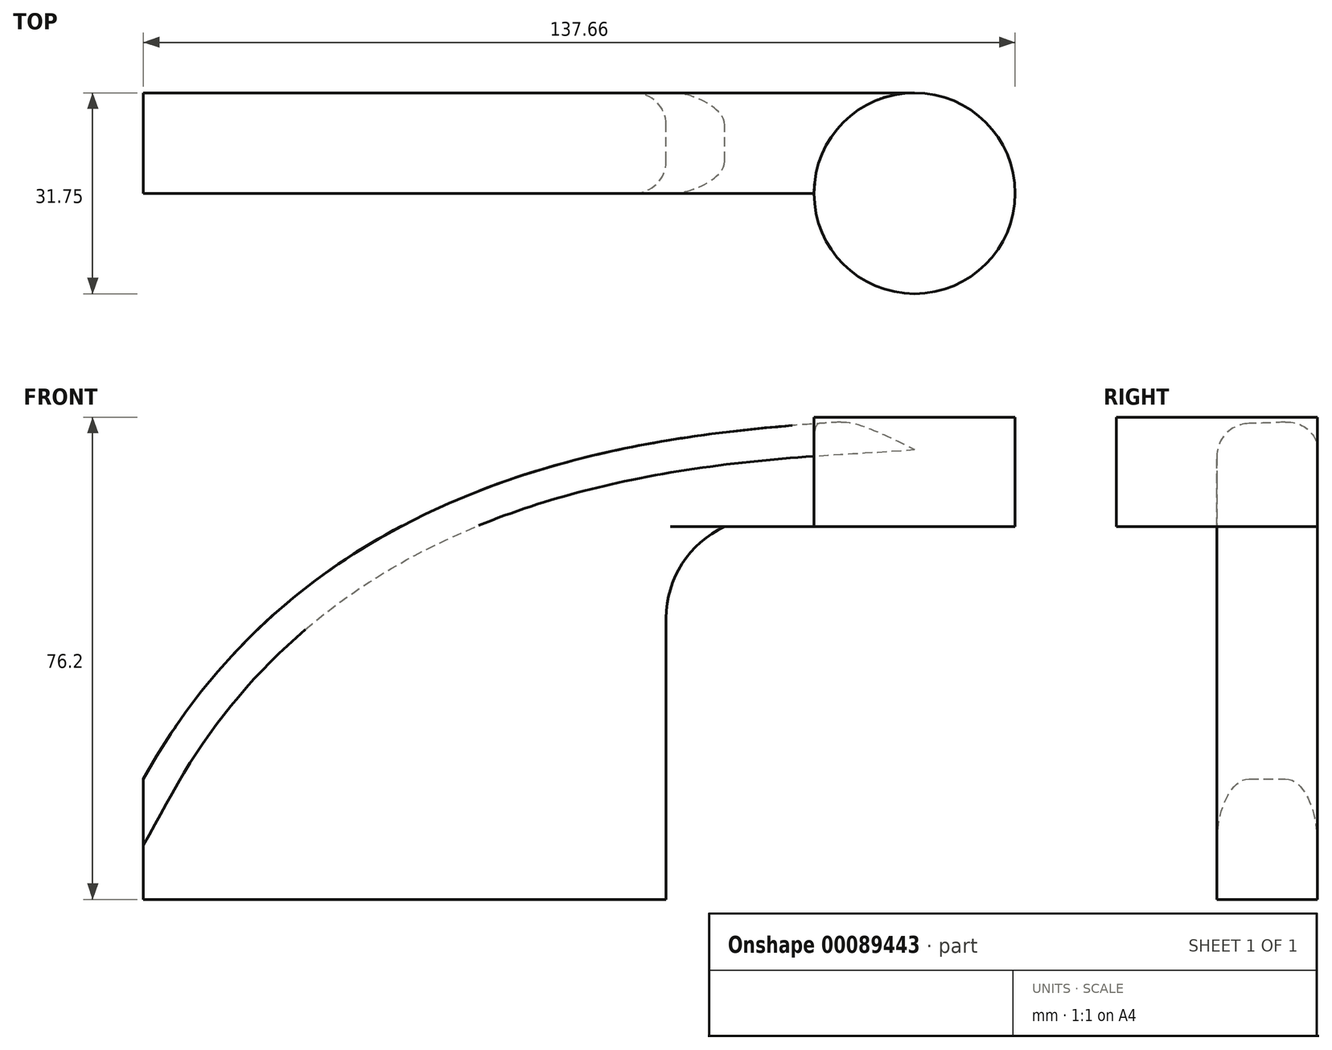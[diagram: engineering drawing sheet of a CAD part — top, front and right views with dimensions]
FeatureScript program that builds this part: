
annotation { "Feature Type Name" : "Feature", "Feature Type Description" : "" }
export const myFeature = defineFeature(function(context is Context, id is Id, definition is map)
    precondition{}
    {
        {
            var Q0;
            Q0=qCreatedBy(makeId("Front.planeOp"),FACE);
            var sketch = newSketch(context, id + "F0", { "sketchPlane" : qUnion([Q0])});
            skLineSegment(sketch, "E0.bottom", {"start": v(-87.78, -32.74) * mm, "end": v(-5.23, -32.74) * mm});
            skLineSegment(sketch, "E0.top", {"start": v(-87.78, -13.69) * mm, "end": v(-5.23, -13.69) * mm});
            skLineSegment(sketch, "E0.left", {"start": v(-87.78, -32.74) * mm, "end": v(-87.78, -13.69) * mm});
            skLineSegment(sketch, "E0.right", {"start": v(-5.23, -32.74) * mm, "end": v(-5.23, -13.69) * mm});
            skLineSegment(sketch, "E1.bottom", {"start": v(84.8, 43.46) * mm, "end": v(34, 43.46) * mm});
            skLineSegment(sketch, "E1.top", {"start": v(84.8, 11.71) * mm, "end": v(34, 11.71) * mm});
            skLineSegment(sketch, "E1.left", {"start": v(84.8, 43.46) * mm, "end": v(84.8, 11.71) * mm});
            skLineSegment(sketch, "E1.right", {"start": v(34, 43.46) * mm, "end": v(34, 11.71) * mm});
            skPoint(sketch, "E1.middle", {"position": v(59.4, 27.59) * mm});
            skLineSegment(sketch, "E2", {"start": v(-5.23, -13.69) * mm, "end": v(-5.23, 11.71) * mm});
            skLineSegment(sketch, "E3", {"start": v(69.71, 19.66) * mm, "end": v(111.85, 19.66) * mm});
            skPoint(sketch, "E4.startSnap0", {"position": v(34, 27.59) * mm});
            skArc(sketch, "E5", {"start": v(-5.23, 11.71) * mm, "mid": v(-2.71, 20.29) * mm, "end": v(4.04, 26.15) * mm});
            skLineSegment(sketch, "E6", {"start": v(4.04, 26.15) * mm, "end": v(48.1, 26.15) * mm});
            skLineSegment(sketch, "E7.0", {"start": v(0.72, 45.2) * mm, "end": v(48.1, 45.2) * mm});
            skArc(sketch, "E7.1", {"start": v(-24.28, 11.71) * mm, "mid": v(-17.34, 32.6) * mm, "end": v(0.72, 45.2) * mm});
            skLineSegment(sketch, "E7.2", {"start": v(-24.28, -13.69) * mm, "end": v(-24.28, 11.71) * mm});
            skLineSegment(sketch, "E8", {"start": v(48.1, 11.71) * mm, "end": v(48.1, 45.2) * mm});
            skFitSpline(sketch, "E9", {"points": [v(-87.78, -13.69) * mm, v(34, 43.46) * mm, v(48.1, 45.2) * mm], "startDerivative": vector(126, 227.65) * mm, "endDerivative": vector(44.75, -1.35) * mm});
            skSolve(sketch);
        }
        {
            var Q0;
            Q0=makeQuery(id+"F0.imprint","IMPRINT",FACE,{"disambiguationData":[TD([[makeQuery(id+"F0.imprint","IMPRINT",EDGE,{"derivedFrom":sQuery(id+"F0.wireOp",EDGE,"E0.bottom")}),1.0]])]});
            var Q1;
            {var subQ1=sQuery(id+"F0.wireOp",EDGE,"E2");Q1=makeQuery(id+"F0.imprint","IMPRINT",FACE,{"disambiguationData":[TD([[makeQuery(id+"F0.imprint","IMPRINT",EDGE,{"derivedFrom":subQ1}),1.0]])]});}
            var Q2;
            {var subQ3=sQuery(id+"F0.wireOp",EDGE,"E7.2");Q2=makeQuery(id+"F0.imprint","IMPRINT",FACE,{"disambiguationData":[TD([[makeQuery(id+"F0.imprint","IMPRINT",EDGE,{"derivedFrom":subQ3}),1.0]])]});}
            extrude(context, id + "F1", {"entities" : qUnion([Q0, Q1, Q2]), "endBound" : BoundingType.SYMMETRIC, "depth" : 15.88 * mm});
        }
        {
            var Q0;
            Q0=makeQuery(id+"F1.opExtrude","SWEPT_FACE",FACE,{"disambiguationData":[OSD([sQuery(id+"F0.wireOp",EDGE,"E1.right")])]});
            var Q1;
            Q1=makeQuery(id+"F1.opExtrude","CAP_EDGE",EDGE,{"disambiguationData":[OSD([sQuery(id+"F0.wireOp",EDGE,"E1.right")])],"isStart":false});
            revolve(context, id + "F2", {"operationType" : NewBodyOperationType.ADD, "entities" : qUnion([Q0]), "axis" : qUnion([Q1]), "revolveType" : RevolveType.FULL});
        }
        {
            var Q0;
            Q0=makeQuery(id+"F1.opExtrude","CAP_EDGE",EDGE,{"disambiguationData":[OSD([sQuery(id+"F0.wireOp",EDGE,"E0.right"),sQuery(id+"F0.wireOp",EDGE,"E2")])],"isStart":false});
            var Q1;
            Q1=makeQuery(id+"F1.opExtrude","CAP_EDGE",EDGE,{"disambiguationData":[OSD([sQuery(id+"F0.wireOp",EDGE,"E0.right"),sQuery(id+"F0.wireOp",EDGE,"E2")])],"isStart":true});
            var Q2;
            Q2=makeQuery(id+"F1.opExtrude","CAP_EDGE",EDGE,{"disambiguationData":[OSD([sQuery(id+"F0.wireOp",EDGE,"E9")])],"isStart":false});
            var Q3;
            Q3=makeQuery(id+"F1.opExtrude","CAP_EDGE",EDGE,{"disambiguationData":[OSD([sQuery(id+"F0.wireOp",EDGE,"E9")])],"isStart":true});
            fillet(context, id + "F3", {"entities" : qUnion([Q0, Q1, Q2, Q3]), "radius" : 5.08 * mm, "tangentPropagation" : true, "allowEdgeOverflow" : false});
        }
    });
